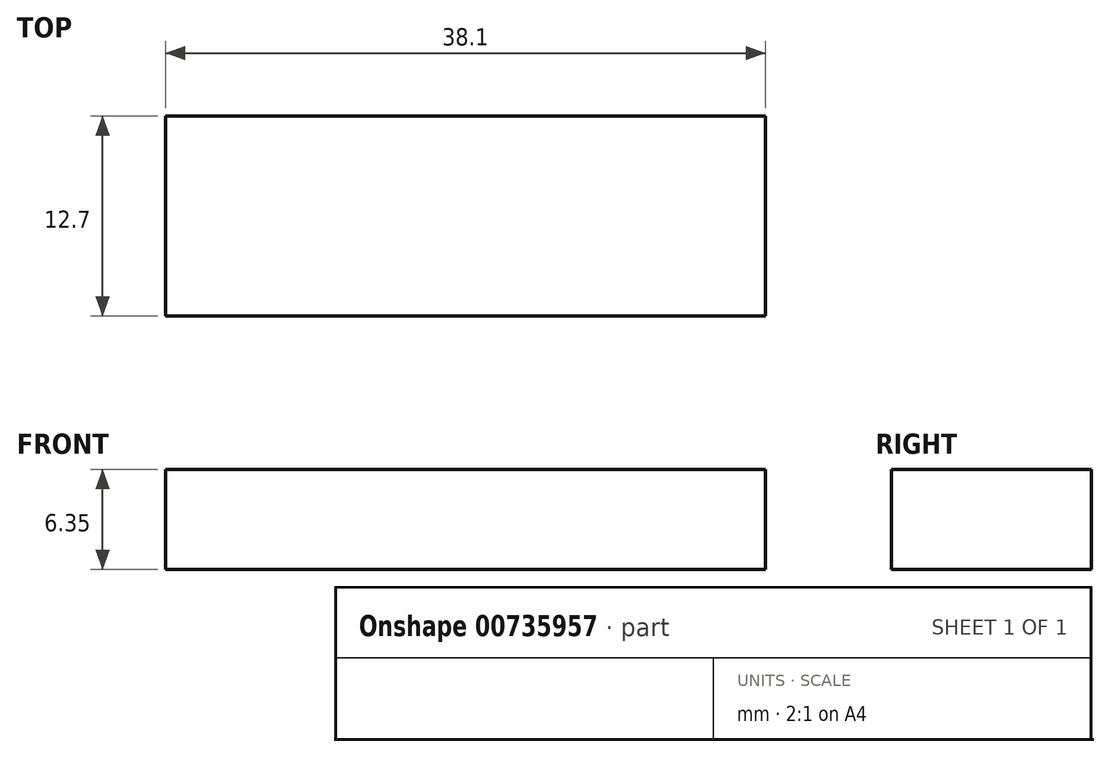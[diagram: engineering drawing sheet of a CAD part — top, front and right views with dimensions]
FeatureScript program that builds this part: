
annotation { "Feature Type Name" : "Feature", "Feature Type Description" : "" }
export const myFeature = defineFeature(function(context is Context, id is Id, definition is map)
    precondition{}
    {
        {
            var Q0;
            Q0=qCreatedBy(makeId("Top.planeOp"),FACE);
            var sketch = newSketch(context, id + "F0", { "sketchPlane" : qUnion([Q0])});
            skLineSegment(sketch, "E0.bottom", {"start": v(19.05, -6.35) * mm, "end": v(-19.05, -6.35) * mm});
            skLineSegment(sketch, "E0.top", {"start": v(19.05, 6.35) * mm, "end": v(-19.05, 6.35) * mm});
            skLineSegment(sketch, "E0.left", {"start": v(19.05, -6.35) * mm, "end": v(19.05, 6.35) * mm});
            skLineSegment(sketch, "E0.right", {"start": v(-19.05, -6.35) * mm, "end": v(-19.05, 6.35) * mm});
            skPoint(sketch, "E0.middle", {"position": v(0, 0) * mm});
            skSolve(sketch);
        }
        {
            var Q0;
            Q0=makeQuery(id+"F0.imprint","IMPRINT",FACE,{"disambiguationData":[TD([[makeQuery(id+"F0.imprint","IMPRINT",EDGE,{"derivedFrom":sQuery(id+"F0.wireOp",EDGE,"E0.bottom")}),-1.0]])]});
            extrude(context, id + "F1", {"entities" : qUnion([Q0]), "depth" : 6.35 * mm, "offsetDistance" : 25.4 * mm});
        }
    });
